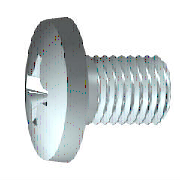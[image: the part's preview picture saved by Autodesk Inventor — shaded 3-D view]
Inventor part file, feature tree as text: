
AUTODESK INVENTOR PART (.ipt)
format: ipt  version: 2014 (Build 180170000, 170)  size: 254,976 bytes
history: native  units: mm (DEFAULTED — no unit token found)
features: other x2, extrude x1, plane x1
ambient origin geometry x7: Origin, YZ Plane, XZ Plane, X Axis, Y Axis, Z Axis, Center Point
bodies: Solid1 (feature_tree), Body (feature_tree)
feature tree (4):
  other  "IDS_WORKPLANE{1}"
  extrude  "Slot"  Depth=2.8448mm
  other  "Cut"
  plane  "Work Plane3"
